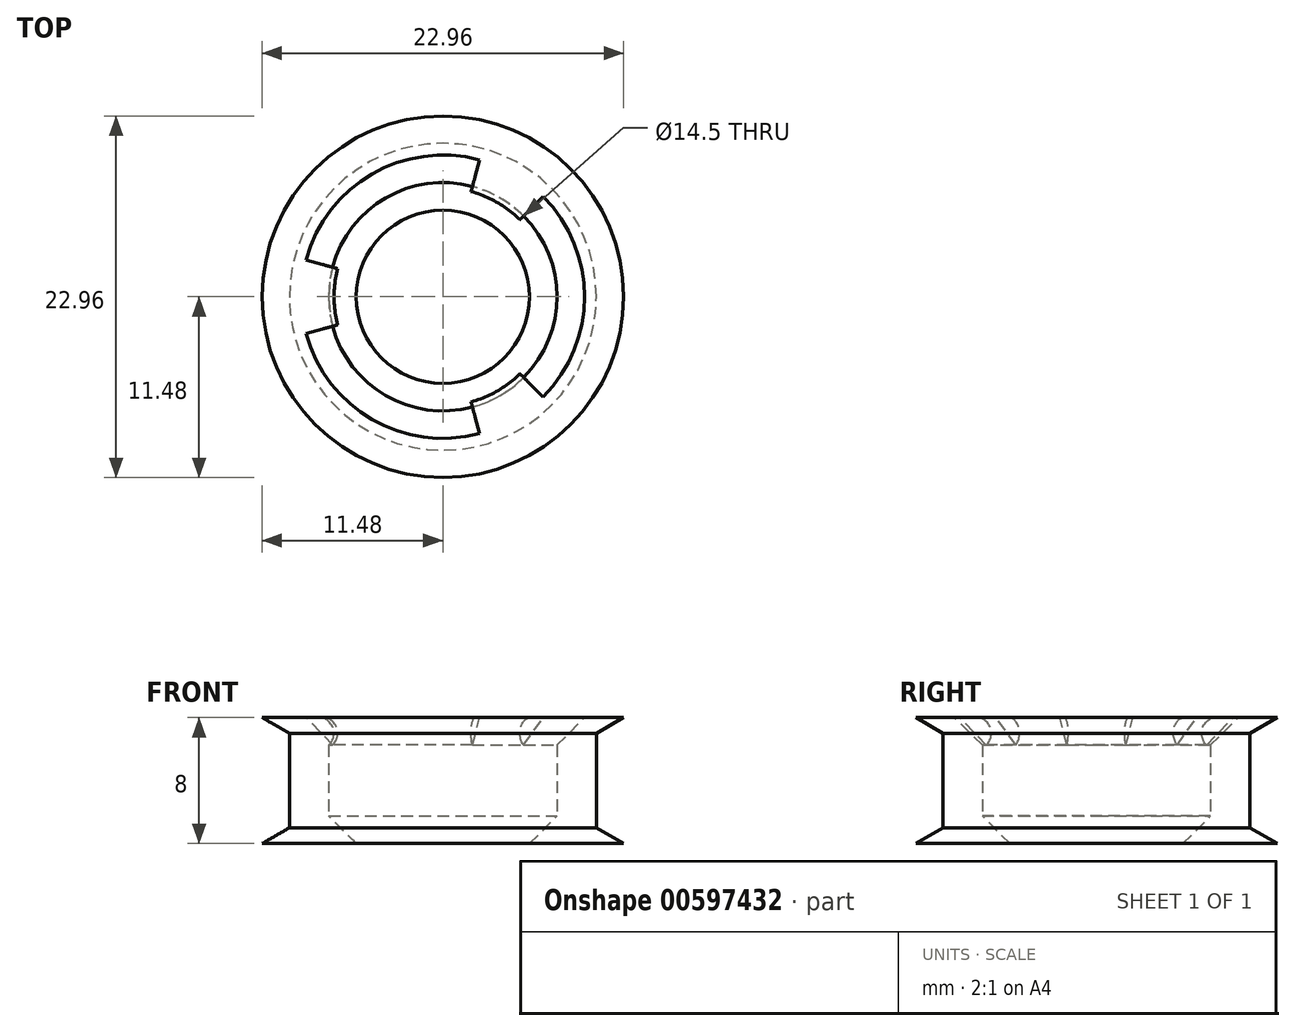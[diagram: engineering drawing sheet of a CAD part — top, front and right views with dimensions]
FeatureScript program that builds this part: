
annotation { "Feature Type Name" : "Feature", "Feature Type Description" : "" }
export const myFeature = defineFeature(function(context is Context, id is Id, definition is map)
    precondition{}
    {
        {
            var Q0;
            Q0=qCreatedBy(makeId("Front.planeOp"),FACE);
            var sketch = newSketch(context, id + "F0", { "sketchPlane" : qUnion([Q0])});
            skLineSegment(sketch, "E0", {"start": v(-7.25, 2.25) * mm, "end": v(-7.25, -2.25) * mm});
            skLineSegment(sketch, "E1", {"start": v(-7.25, -2.25) * mm, "end": v(-5.5, -4) * mm});
            skLineSegment(sketch, "E2", {"start": v(-7.25, 2.25) * mm, "end": v(-9, 4) * mm});
            skLineSegment(sketch, "E3", {"start": v(-9, 4) * mm, "end": v(-11.48, 4) * mm});
            skLineSegment(sketch, "E4", {"start": v(-11.48, 4) * mm, "end": v(-9.75, 3) * mm});
            skLineSegment(sketch, "E5", {"start": v(-9.75, 3) * mm, "end": v(-9.75, -3) * mm});
            skLineSegment(sketch, "E6", {"start": v(-9.75, -3) * mm, "end": v(-11.48, -4) * mm});
            skLineSegment(sketch, "E7", {"start": v(-11.48, -4) * mm, "end": v(-5.5, -4) * mm});
            skLineSegment(sketch, "E8", {"start": v(0, -4) * mm, "end": v(0, 4) * mm, "construction": true});
            skPoint(sketch, "E9", {"position": v(-9.75, 0) * mm});
            skPoint(sketch, "E10", {"position": v(-7.25, 0) * mm});
            skLineSegment(sketch, "E11.MirrorCS", {"start": v(11.48, -4) * mm, "end": v(5.5, -4) * mm});
            skLineSegment(sketch, "E12.MirrorCS", {"start": v(7.25, -2.25) * mm, "end": v(5.5, -4) * mm});
            skLineSegment(sketch, "E13.MirrorCS", {"start": v(7.25, 2.25) * mm, "end": v(7.25, -2.25) * mm});
            skLineSegment(sketch, "E14.MirrorCS", {"start": v(7.25, 2.25) * mm, "end": v(9, 4) * mm});
            skLineSegment(sketch, "E15.MirrorCS", {"start": v(9, 4) * mm, "end": v(11.48, 4) * mm});
            skLineSegment(sketch, "E16.MirrorCS", {"start": v(11.48, 4) * mm, "end": v(9.75, 3) * mm});
            skLineSegment(sketch, "E17.MirrorCS", {"start": v(9.75, 3) * mm, "end": v(9.75, -3) * mm});
            skLineSegment(sketch, "E18.MirrorCS", {"start": v(9.75, -3) * mm, "end": v(11.48, -4) * mm});
            skLineSegment(sketch, "E19", {"start": v(-7.25, 2.25) * mm, "end": v(-5.5, 4) * mm});
            skLineSegment(sketch, "E20", {"start": v(-5.5, 4) * mm, "end": v(-9, 4) * mm});
            skLineSegment(sketch, "E21.MirrorCS", {"start": v(7.25, 2.25) * mm, "end": v(5.5, 4) * mm});
            skLineSegment(sketch, "E22.MirrorCS", {"start": v(5.5, 4) * mm, "end": v(9, 4) * mm});
            skSolve(sketch);
        }
        {
            var Q0;
            Q0=makeQuery(id+"F0.imprint","IMPRINT",FACE,{"disambiguationData":[TD([[makeQuery(id+"F0.imprint","IMPRINT",EDGE,{"derivedFrom":sQuery(id+"F0.wireOp",EDGE,"E0")}),-1.0]])]});
            var Q1;
            Q1=sQuery(id+"F0.wireOp",EDGE,"E8");
            revolve(context, id + "F1", {"entities" : qUnion([Q0]), "axis" : qUnion([Q1]), "revolveType" : RevolveType.FULL});
        }
        {
            var Q0;
            Q0=makeQuery(id+"F0.imprint","IMPRINT",FACE,{"disambiguationData":[TD([[makeQuery(id+"F0.imprint","IMPRINT",EDGE,{"derivedFrom":sQuery(id+"F0.wireOp",EDGE,"E2")}),-1.0]])]});
            var Q1;
            Q1=sQuery(id+"F0.wireOp",EDGE,"E8");
            revolve(context, id + "F2", {"entities" : qUnion([Q0]), "axis" : qUnion([Q1]), "revolveType" : RevolveType.SYMMETRIC, "angle" : 30 * degree});
        }
        {
            var Q0;
            Q0=makeQuery(id+"F2.opRevolve","SWEPT_BODY",BODY,{"disambiguationData":[OSD([sQuery(id+"F0.wireOp",EDGE,"E2"),sQuery(id+"F0.wireOp",EDGE,"E19"),sQuery(id+"F0.wireOp",EDGE,"E20")])]});
            var Q1;
            Q1=sQuery(id+"F0.wireOp",EDGE,"E8");
            circularPattern(context, id + "F3", {"operationType" : NewBodyOperationType.ADD, "entities" : qUnion([Q0]), "axis" : qUnion([Q1]), "angle" : 360 * degree, "instanceCount" : 3, "equalSpace" : true});
        }
        {
            var Q0;
            Q0=makeQuery(id+"F3.opPattern","COPY",EDGE,{"derivedFrom":makeQuery(id+"F2.opRevolve","SWEPT_EDGE",EDGE,{"disambiguationData":[OSD([sQuery(id+"F0.wireOp",EDGE,"E19"),sQuery(id+"F0.wireOp",EDGE,"E20")])]}),"instanceName":"2"});
            var Q1;
            Q1=makeQuery(id+"F2.opRevolve","SWEPT_EDGE",EDGE,{"disambiguationData":[OSD([sQuery(id+"F0.wireOp",EDGE,"E19"),sQuery(id+"F0.wireOp",EDGE,"E20")])]});
            var Q2;
            Q2=makeQuery(id+"F3.opPattern","COPY",EDGE,{"derivedFrom":makeQuery(id+"F2.opRevolve","SWEPT_EDGE",EDGE,{"disambiguationData":[OSD([sQuery(id+"F0.wireOp",EDGE,"E19"),sQuery(id+"F0.wireOp",EDGE,"E20")])]}),"instanceName":"1"});
            fillet(context, id + "F4", {"entities" : qUnion([Q0, Q1, Q2]), "radius" : 1 * mm, "tangentPropagation" : true, "allowEdgeOverflow" : false});
        }
    });
